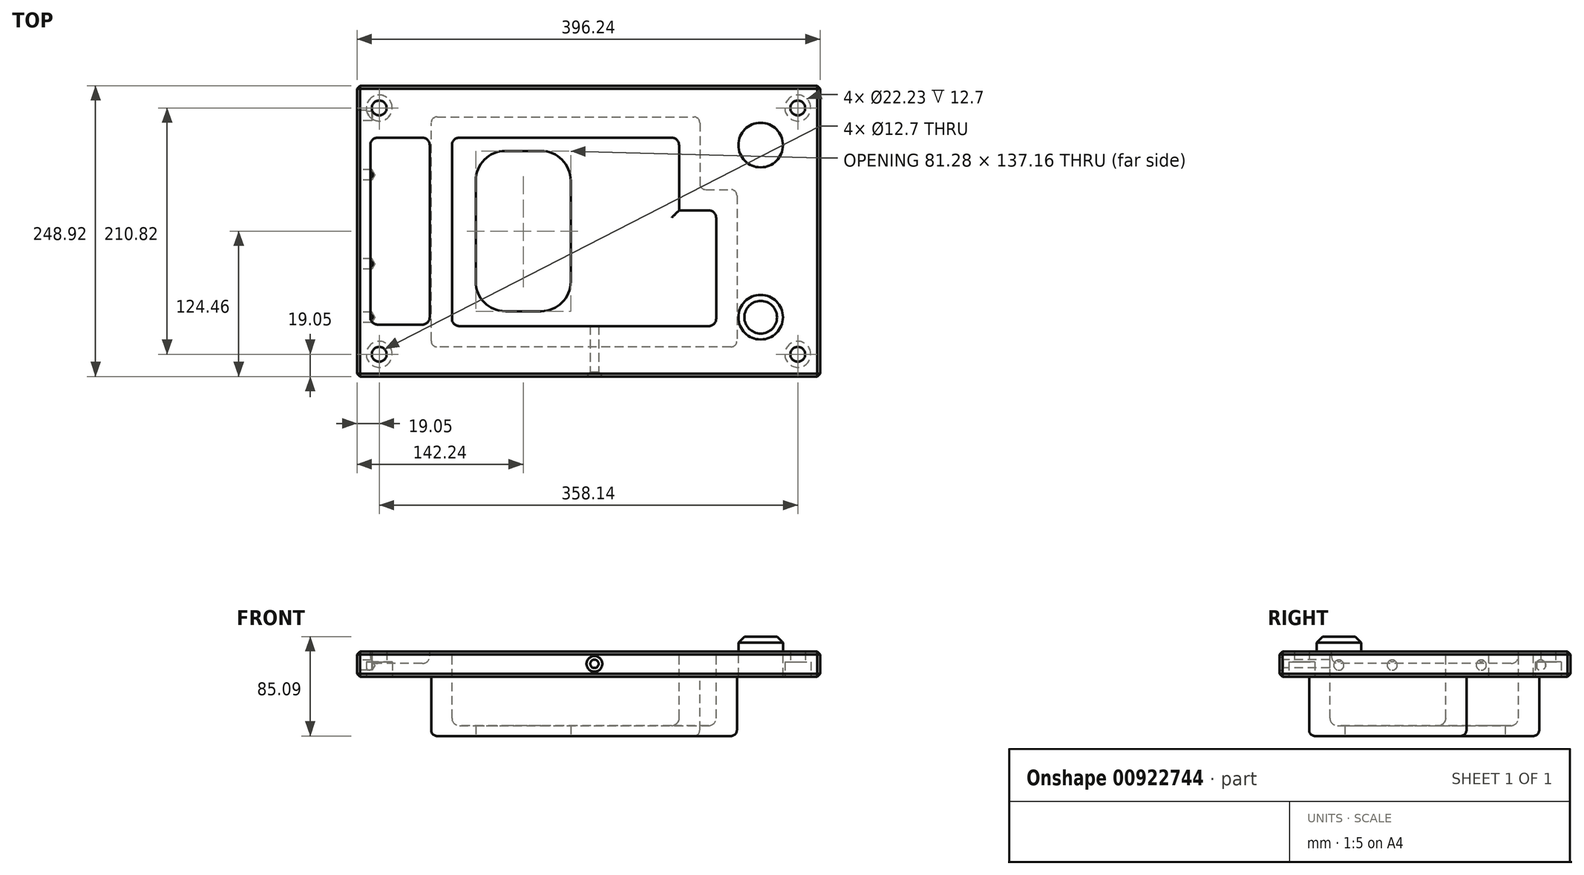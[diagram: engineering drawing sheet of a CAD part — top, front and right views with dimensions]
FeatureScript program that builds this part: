
annotation { "Feature Type Name" : "Feature", "Feature Type Description" : "" }
export const myFeature = defineFeature(function(context is Context, id is Id, definition is map)
    precondition{}
    {
        {
            var Q0;
            Q0=qCreatedBy(makeId("Top.planeOp"),FACE);
            var sketch = newSketch(context, id + "F0", { "sketchPlane" : qUnion([Q0])});
            skLineSegment(sketch, "E0.bottom", {"start": v(198.12, 124.46) * mm, "end": v(-198.12, 124.46) * mm});
            skLineSegment(sketch, "E0.top", {"start": v(198.12, -124.46) * mm, "end": v(-198.12, -124.46) * mm});
            skLineSegment(sketch, "E0.left", {"start": v(198.12, 124.46) * mm, "end": v(198.12, -124.46) * mm});
            skLineSegment(sketch, "E0.right", {"start": v(-198.12, 124.46) * mm, "end": v(-198.12, -124.46) * mm});
            skPoint(sketch, "E0.middle", {"position": v(0, 0) * mm});
            skSolve(sketch);
        }
        {
            var Q0;
            Q0=qSketchRegion(id+"F0",true);
            extrude(context, id + "F1", {"entities" : qUnion([Q0]), "oppositeDirection" : true, "depth" : 21.59 * mm, "offsetDistance" : 25.4 * mm});
        }
        {
            var Q0;
            Q0=makeQuery(id+"F1.opExtrude","CAP_FACE",FACE,{"disambiguationData":[OSD([sQuery(id+"F0.wireOp",EDGE,"E0.bottom"),sQuery(id+"F0.wireOp",EDGE,"E0.top"),sQuery(id+"F0.wireOp",EDGE,"E0.left"),sQuery(id+"F0.wireOp",EDGE,"E0.right")])],"isStart":false});
            var sketch = newSketch(context, id + "F2", { "sketchPlane" : qUnion([Q0])});
            skLineSegment(sketch, "E1", {"start": v(-134.62, 99.06) * mm, "end": v(-134.62, -97.79) * mm});
            skLineSegment(sketch, "E2", {"start": v(-134.62, -97.79) * mm, "end": v(95.25, -97.79) * mm});
            skLineSegment(sketch, "E3", {"start": v(95.25, -97.8) * mm, "end": v(95.25, -35.56) * mm});
            skLineSegment(sketch, "E4", {"start": v(95.25, -35.56) * mm, "end": v(127, -35.56) * mm});
            skLineSegment(sketch, "E5", {"start": v(127, -35.56) * mm, "end": v(127, 99.06) * mm});
            skLineSegment(sketch, "E6", {"start": v(127, 99.06) * mm, "end": v(-134.62, 99.06) * mm});
            skSolve(sketch);
        }
        {
            var Q0;
            Q0=qSketchRegion(id+"F2",true);
            extrude(context, id + "F3", {"entities" : qUnion([Q0]), "operationType" : NewBodyOperationType.ADD, "depth" : 50.8 * mm, "offsetDistance" : 25.4 * mm});
        }
        {
            var Q0;
            Q0=makeQuery(id+"F1.opExtrude","CAP_FACE",FACE,{"disambiguationData":[OSD([sQuery(id+"F0.wireOp",EDGE,"E0.bottom"),sQuery(id+"F0.wireOp",EDGE,"E0.top"),sQuery(id+"F0.wireOp",EDGE,"E0.left"),sQuery(id+"F0.wireOp",EDGE,"E0.right")])],"isStart":true});
            var sketch = newSketch(context, id + "F4", { "sketchPlane" : qUnion([Q0])});
            skLineSegment(sketch, "E7.0", {"start": v(127, -99.06) * mm, "end": v(-134.62, -99.06) * mm, "construction": true});
            skLineSegment(sketch, "E8.0", {"start": v(127, 35.56) * mm, "end": v(127, -99.06) * mm, "construction": true});
            skPoint(sketch, "E9.0", {"position": v(111.12, 35.56) * mm});
            skLineSegment(sketch, "E10.0", {"start": v(95.25, 97.8) * mm, "end": v(95.25, 35.56) * mm, "construction": true});
            skLineSegment(sketch, "E11.0", {"start": v(95.25, 35.56) * mm, "end": v(127, 35.56) * mm, "construction": true});
            skLineSegment(sketch, "E12.0", {"start": v(-134.62, 97.79) * mm, "end": v(95.25, 97.79) * mm, "construction": true});
            skLineSegment(sketch, "E13.0", {"start": v(-134.62, -99.06) * mm, "end": v(-134.62, 97.79) * mm, "construction": true});
            skLineSegment(sketch, "E14", {"start": v(109.22, -81.28) * mm, "end": v(109.22, 17.78) * mm});
            skLineSegment(sketch, "E15", {"start": v(109.22, 17.78) * mm, "end": v(77.47, 17.78) * mm});
            skLineSegment(sketch, "E16", {"start": v(77.47, 17.78) * mm, "end": v(77.47, 80) * mm});
            skLineSegment(sketch, "E17", {"start": v(77.47, 80) * mm, "end": v(-116.84, 80) * mm});
            skLineSegment(sketch, "E18", {"start": v(-116.84, 80) * mm, "end": v(-116.84, -81.28) * mm});
            skLineSegment(sketch, "E19", {"start": v(-116.84, -81.28) * mm, "end": v(109.22, -81.28) * mm});
            skSolve(sketch);
        }
        {
            var Q0;
            Q0=qSketchRegion(id+"F4",true);
            extrude(context, id + "F5", {"entities" : qUnion([Q0]), "operationType" : NewBodyOperationType.REMOVE, "oppositeDirection" : true, "depth" : 63.5 * mm, "offsetDistance" : 25.4 * mm});
        }
        {
            var Q0;
            Q0=makeQuery(id+"F5.boolean.opBoolean","COPY",FACE,{"derivedFrom":makeQuery(id+"F5.opExtrude","CAP_FACE",FACE,{"disambiguationData":[OSD([sQuery(id+"F4.wireOp",EDGE,"E14"),sQuery(id+"F4.wireOp",EDGE,"E15"),sQuery(id+"F4.wireOp",EDGE,"E16"),sQuery(id+"F4.wireOp",EDGE,"E17"),sQuery(id+"F4.wireOp",EDGE,"E18"),sQuery(id+"F4.wireOp",EDGE,"E19")])],"isStart":false})});
            var Q1;
            Q1=makeQuery(id+"F5.boolean.opBoolean","COPY",EDGE,{"derivedFrom":makeQuery(id+"F5.opExtrude","SWEPT_EDGE",EDGE,{"disambiguationData":[OSD([sQuery(id+"F4.wireOp",EDGE,"E14"),sQuery(id+"F4.wireOp",EDGE,"E19")])]})});
            var Q2;
            Q2=makeQuery(id+"F5.boolean.opBoolean","COPY",EDGE,{"derivedFrom":makeQuery(id+"F5.opExtrude","SWEPT_EDGE",EDGE,{"disambiguationData":[OSD([sQuery(id+"F4.wireOp",EDGE,"E18"),sQuery(id+"F4.wireOp",EDGE,"E19")])]})});
            var Q3;
            Q3=makeQuery(id+"F5.boolean.opBoolean","COPY",EDGE,{"derivedFrom":makeQuery(id+"F5.opExtrude","SWEPT_EDGE",EDGE,{"disambiguationData":[OSD([sQuery(id+"F4.wireOp",EDGE,"E17"),sQuery(id+"F4.wireOp",EDGE,"E18")])]})});
            var Q4;
            Q4=makeQuery(id+"F5.boolean.opBoolean","COPY",EDGE,{"derivedFrom":makeQuery(id+"F5.opExtrude","SWEPT_EDGE",EDGE,{"disambiguationData":[OSD([sQuery(id+"F4.wireOp",EDGE,"E14"),sQuery(id+"F4.wireOp",EDGE,"E15")])]})});
            var Q5;
            Q5=makeQuery(id+"F5.boolean.opBoolean","COPY",EDGE,{"derivedFrom":makeQuery(id+"F5.opExtrude","SWEPT_EDGE",EDGE,{"disambiguationData":[OSD([sQuery(id+"F4.wireOp",EDGE,"E16"),sQuery(id+"F4.wireOp",EDGE,"E17")])]})});
            fillet(context, id + "F6", {"entities" : qUnion([Q0, Q1, Q2, Q3, Q4, Q5]), "radius" : 6.35 * mm, "tangentPropagation" : true, "allowEdgeOverflow" : false});
        }
        {
            var Q0;
            Q0=makeQuery(id+"F3.opExtrude","SWEPT_EDGE",EDGE,{"disambiguationData":[OSD([sQuery(id+"F2.wireOp",EDGE,"E3"),sQuery(id+"F2.wireOp",EDGE,"E4")])]});
            fillet(context, id + "F7", {"entities" : qUnion([Q0]), "radius" : 5.08 * mm, "tangentPropagation" : true, "allowEdgeOverflow" : false});
        }
        {
            var Q0;
            Q0=makeQuery(id+"F3.opExtrude","CAP_FACE",FACE,{"disambiguationData":[OSD([sQuery(id+"F2.wireOp",EDGE,"E1"),sQuery(id+"F2.wireOp",EDGE,"E2"),sQuery(id+"F2.wireOp",EDGE,"E3"),sQuery(id+"F2.wireOp",EDGE,"E4"),sQuery(id+"F2.wireOp",EDGE,"E5"),sQuery(id+"F2.wireOp",EDGE,"E6")])],"isStart":false});
            var sketch = newSketch(context, id + "F8", { "sketchPlane" : qUnion([Q0])});
            skLineSegment(sketch, "E20.bottom", {"start": v(-96.52, -68.58) * mm, "end": v(-15.24, -68.58) * mm});
            skLineSegment(sketch, "E20.top", {"start": v(-96.52, 68.58) * mm, "end": v(-15.24, 68.58) * mm});
            skLineSegment(sketch, "E20.left", {"start": v(-96.52, -68.58) * mm, "end": v(-96.52, 68.58) * mm});
            skLineSegment(sketch, "E20.right", {"start": v(-15.24, -68.58) * mm, "end": v(-15.24, 68.58) * mm});
            skPoint(sketch, "E20.middle", {"position": v(-55.88, 0) * mm});
            skSolve(sketch);
        }
        {
            var Q0;
            Q0=qSketchRegion(id+"F8",true);
            extrude(context, id + "F9", {"entities" : qUnion([Q0]), "operationType" : NewBodyOperationType.REMOVE, "endBound" : BoundingType.THROUGH_ALL, "oppositeDirection" : true, "depth" : 25.4 * mm, "offsetDistance" : 25.4 * mm});
        }
        {
            var Q0;
            Q0=makeQuery(id+"F1.opExtrude","CAP_FACE",FACE,{"disambiguationData":[OSD([sQuery(id+"F0.wireOp",EDGE,"E0.bottom"),sQuery(id+"F0.wireOp",EDGE,"E0.top"),sQuery(id+"F0.wireOp",EDGE,"E0.left"),sQuery(id+"F0.wireOp",EDGE,"E0.right")])],"isStart":true});
            var sketch = newSketch(context, id + "F10", { "sketchPlane" : qUnion([Q0])});
            skLineSegment(sketch, "E21.bottom", {"start": v(-135.9, 80) * mm, "end": v(-186.7, 80) * mm});
            skLineSegment(sketch, "E21.top", {"start": v(-135.9, -80) * mm, "end": v(-186.7, -80) * mm});
            skLineSegment(sketch, "E21.left", {"start": v(-135.9, 80) * mm, "end": v(-135.9, -80) * mm});
            skLineSegment(sketch, "E21.right", {"start": v(-186.7, 80) * mm, "end": v(-186.7, -80) * mm});
            skPoint(sketch, "E21.middle", {"position": v(-161.3, 0) * mm});
            skSolve(sketch);
        }
        {
            var Q0;
            Q0=qSketchRegion(id+"F10",true);
            extrude(context, id + "F11", {"entities" : qUnion([Q0]), "operationType" : NewBodyOperationType.REMOVE, "oppositeDirection" : true, "depth" : 10.4 * mm, "offsetDistance" : 25.4 * mm});
        }
        {
            var Q0;
            Q0=makeQuery(id+"F11.boolean.opBoolean","COPY",FACE,{"derivedFrom":makeQuery(id+"F11.opExtrude","CAP_FACE",FACE,{"disambiguationData":[OSD([sQuery(id+"F10.wireOp",EDGE,"E21.bottom"),sQuery(id+"F10.wireOp",EDGE,"E21.top"),sQuery(id+"F10.wireOp",EDGE,"E21.left"),sQuery(id+"F10.wireOp",EDGE,"E21.right")])],"isStart":false})});
            var Q1;
            Q1=makeQuery(id+"F11.boolean.opBoolean","COPY",EDGE,{"derivedFrom":makeQuery(id+"F11.opExtrude","SWEPT_EDGE",EDGE,{"disambiguationData":[OSD([sQuery(id+"F10.wireOp",EDGE,"E21.bottom"),sQuery(id+"F10.wireOp",EDGE,"E21.right")])]})});
            var Q2;
            Q2=makeQuery(id+"F11.boolean.opBoolean","COPY",EDGE,{"derivedFrom":makeQuery(id+"F11.opExtrude","SWEPT_EDGE",EDGE,{"disambiguationData":[OSD([sQuery(id+"F10.wireOp",EDGE,"E21.bottom"),sQuery(id+"F10.wireOp",EDGE,"E21.left")])]})});
            var Q3;
            Q3=makeQuery(id+"F11.boolean.opBoolean","COPY",EDGE,{"derivedFrom":makeQuery(id+"F11.opExtrude","SWEPT_EDGE",EDGE,{"disambiguationData":[OSD([sQuery(id+"F10.wireOp",EDGE,"E21.top"),sQuery(id+"F10.wireOp",EDGE,"E21.left")])]})});
            var Q4;
            Q4=makeQuery(id+"F11.boolean.opBoolean","COPY",EDGE,{"derivedFrom":makeQuery(id+"F11.opExtrude","SWEPT_EDGE",EDGE,{"disambiguationData":[OSD([sQuery(id+"F10.wireOp",EDGE,"E21.top"),sQuery(id+"F10.wireOp",EDGE,"E21.right")])]})});
            fillet(context, id + "F12", {"entities" : qUnion([Q0, Q1, Q2, Q3, Q4]), "radius" : 6.35 * mm, "tangentPropagation" : true, "allowEdgeOverflow" : false});
        }
        {
            var Q0;
            Q0=makeQuery(id+"F1.opExtrude","CAP_FACE",FACE,{"disambiguationData":[OSD([sQuery(id+"F0.wireOp",EDGE,"E0.bottom"),sQuery(id+"F0.wireOp",EDGE,"E0.top"),sQuery(id+"F0.wireOp",EDGE,"E0.left"),sQuery(id+"F0.wireOp",EDGE,"E0.right")])],"isStart":true});
            var sketch = newSketch(context, id + "F13", { "sketchPlane" : qUnion([Q0])});
            skLineSegment(sketch, "E22.bottom", {"start": v(160.02, 86.36) * mm, "end": v(134.62, 86.36) * mm});
            skLineSegment(sketch, "E22.top", {"start": v(160.02, 60.96) * mm, "end": v(134.62, 60.96) * mm});
            skLineSegment(sketch, "E22.left", {"start": v(160.02, 86.36) * mm, "end": v(160.02, 60.96) * mm});
            skLineSegment(sketch, "E22.right", {"start": v(134.62, 86.36) * mm, "end": v(134.62, 60.96) * mm});
            skPoint(sketch, "E22.middle", {"position": v(147.32, 73.66) * mm});
            skCircle(sketch, "E23", {"center": v(147.32, -73.66) * mm, "radius": 19.05 * mm});
            skSolve(sketch);
        }
        {
            var Q0;
            Q0=makeQuery(id+"F13.imprint","IMPRINT",FACE,{"disambiguationData":[TD([[makeQuery(id+"F13.imprint","IMPRINT",EDGE,{"derivedFrom":sQuery(id+"F13.wireOp",EDGE,"E23")}),1.0]])]});
            extrude(context, id + "F14", {"entities" : qUnion([Q0]), "operationType" : NewBodyOperationType.ADD, "depth" : 12.7 * mm, "offsetDistance" : 25.4 * mm});
        }
        {
            var Q0;
            Q0=makeQuery(id+"F14.opExtrude","CAP_FACE",FACE,{"disambiguationData":[OSD([sQuery(id+"F13.wireOp",EDGE,"E22.bottom"),sQuery(id+"F13.wireOp",EDGE,"E22.top"),sQuery(id+"F13.wireOp",EDGE,"E22.left"),sQuery(id+"F13.wireOp",EDGE,"E22.right")])],"isStart":false});
            var Q1;
            Q1=makeQuery(id+"F14.opExtrude","CAP_FACE",FACE,{"disambiguationData":[OSD([sQuery(id+"F13.wireOp",EDGE,"E23")])],"isStart":false});
            chamfer(context, id + "F15", {"entities" : qUnion([Q0, Q1]), "width" : 5.08 * mm, "tangentPropagation" : true});
        }
        {
            var Q0;
            Q0=makeQuery(id+"F1.opExtrude","SWEPT_FACE",FACE,{"disambiguationData":[OSD([sQuery(id+"F0.wireOp",EDGE,"E0.top")])]});
            var sketch = newSketch(context, id + "F16", { "sketchPlane" : qUnion([Q0])});
            skPoint(sketch, "E24", {"position": v(5.08, -10.67) * mm});
            skSolve(sketch);
        }
        {
            var Q0;
            Q0=sQuery(id+"F16.wireOp",VERTEX,"E24");
            var Q1;
            Q1=makeQuery(id+"F1.opExtrude","SWEPT_BODY",BODY,{"disambiguationData":[OSD([sQuery(id+"F0.wireOp",EDGE,"E0.bottom"),sQuery(id+"F0.wireOp",EDGE,"E0.top"),sQuery(id+"F0.wireOp",EDGE,"E0.left"),sQuery(id+"F0.wireOp",EDGE,"E0.right")])]});
            hole(context, id + "F17", {"style" : HoleStyle.C_SINK, "endStyle" : HoleEndStyle.BLIND, "standardTappedOrClearance" : lookupTablePath({ "fit" : "Normal (ASME)", "standard" : "ANSI", "size" : "1/4", "type" : "Clearance" }), "standardBlindInLast" : lookupTablePath({ "fit" : "Normal", "standard" : "ANSI", "size" : "1/4", "type" : "Clearance" }), "holeDiameter" : 7.14 * mm, "cSinkDiameter" : 13.5 * mm, "cSinkAngle" : 82 * degree, "majorDiameter" : 6.35 * mm, "holeDepth" : 127 * mm, "isTappedThrough" : true, "tappedDepth" : 12.7 * mm, "tapClearance" : 3, "locations" : qUnion([Q0]), "scope" : qUnion([Q1])});
        }
        {
            var Q0;
            Q0=makeQuery(id+"F3.opExtrude","CAP_EDGE",EDGE,{"disambiguationData":[OSD([sQuery(id+"F2.wireOp",EDGE,"E6")])],"isStart":false});
            var Q1;
            Q1=makeQuery(id+"F3.opExtrude","SWEPT_EDGE",EDGE,{"disambiguationData":[OSD([sQuery(id+"F2.wireOp",EDGE,"E1"),sQuery(id+"F2.wireOp",EDGE,"E6")])]});
            var Q2;
            Q2=makeQuery(id+"F3.opExtrude","CAP_EDGE",EDGE,{"disambiguationData":[OSD([sQuery(id+"F2.wireOp",EDGE,"E1")])],"isStart":false});
            var Q3;
            Q3=makeQuery(id+"F3.opExtrude","CAP_EDGE",EDGE,{"disambiguationData":[OSD([sQuery(id+"F2.wireOp",EDGE,"E5")])],"isStart":false});
            var Q4;
            Q4=makeQuery(id+"F3.opExtrude","SWEPT_EDGE",EDGE,{"disambiguationData":[OSD([sQuery(id+"F2.wireOp",EDGE,"E5"),sQuery(id+"F2.wireOp",EDGE,"E6")])]});
            var Q5;
            Q5=makeQuery(id+"F3.opExtrude","SWEPT_EDGE",EDGE,{"disambiguationData":[OSD([sQuery(id+"F2.wireOp",EDGE,"E4"),sQuery(id+"F2.wireOp",EDGE,"E5")])]});
            var Q6;
            Q6=makeQuery(id+"F3.opExtrude","CAP_EDGE",EDGE,{"disambiguationData":[OSD([sQuery(id+"F2.wireOp",EDGE,"E4")])],"isStart":false});
            var Q7;
            Q7=makeQuery(id+"F3.opExtrude","SWEPT_EDGE",EDGE,{"disambiguationData":[OSD([sQuery(id+"F2.wireOp",EDGE,"E2"),sQuery(id+"F2.wireOp",EDGE,"E3")])]});
            var Q8;
            Q8=makeQuery(id+"F3.opExtrude","CAP_EDGE",EDGE,{"disambiguationData":[OSD([sQuery(id+"F2.wireOp",EDGE,"E2")])],"isStart":false});
            var Q9;
            Q9=makeQuery(id+"F3.opExtrude","SWEPT_EDGE",EDGE,{"disambiguationData":[OSD([sQuery(id+"F2.wireOp",EDGE,"E1"),sQuery(id+"F2.wireOp",EDGE,"E2")])]});
            fillet(context, id + "F18", {"entities" : qUnion([Q0, Q1, Q2, Q3, Q4, Q5, Q6, Q7, Q8, Q9]), "radius" : 5.08 * mm, "tangentPropagation" : true, "allowEdgeOverflow" : false});
        }
        {
            var Q0;
            Q0=makeQuery(id+"F2.imprint","IMPRINT",FACE,{"disambiguationData":[TD([[makeQuery(id+"F2.imprint","IMPRINT",EDGE,{"derivedFrom":sQuery(id+"F2.wireOp",EDGE,"E1")}),-1.0]])]});
            var sketch = newSketch(context, id + "F19", { "sketchPlane" : qUnion([Q0])});
            skLineSegment(sketch, "E25.bottom", {"start": v(179.07, -105.41) * mm, "end": v(-179.07, -105.41) * mm});
            skLineSegment(sketch, "E25.top", {"start": v(179.07, 105.41) * mm, "end": v(-179.07, 105.41) * mm});
            skLineSegment(sketch, "E25.left", {"start": v(179.07, -105.41) * mm, "end": v(179.07, 105.41) * mm});
            skLineSegment(sketch, "E25.right", {"start": v(-179.07, -105.41) * mm, "end": v(-179.07, 105.41) * mm});
            skPoint(sketch, "E25.middle", {"position": v(0, 0) * mm});
            skSolve(sketch);
        }
        {
            var Q0;
            Q0=sQuery(id+"F19.wireOp",VERTEX,"E25.top.end");
            var Q1;
            Q1=sQuery(id+"F19.wireOp",VERTEX,"E25.top.start");
            var Q2;
            Q2=sQuery(id+"F19.wireOp",VERTEX,"E25.bottom.start");
            var Q3;
            Q3=sQuery(id+"F19.wireOp",VERTEX,"E25.bottom.end");
            var Q4;
            Q4=makeQuery(id+"F1.opExtrude","SWEPT_BODY",BODY,{"disambiguationData":[OSD([sQuery(id+"F0.wireOp",EDGE,"E0.bottom"),sQuery(id+"F0.wireOp",EDGE,"E0.top"),sQuery(id+"F0.wireOp",EDGE,"E0.left"),sQuery(id+"F0.wireOp",EDGE,"E0.right")])]});
            hole(context, id + "F20", {"style" : HoleStyle.C_BORE, "endStyle" : HoleEndStyle.THROUGH, "holeDiameter" : 12.7 * mm, "cBoreDiameter" : 22.22 * mm, "cBoreDepth" : 12.7 * mm, "majorDiameter" : 6.35 * mm, "isTappedThrough" : true, "tappedDepth" : 12.7 * mm, "tapClearance" : 3, "locations" : qUnion([Q0, Q1, Q2, Q3]), "scope" : qUnion([Q4])});
        }
        {
            var Q0;
            Q0=makeQuery(id+"F1.opExtrude","CAP_FACE",FACE,{"disambiguationData":[OSD([sQuery(id+"F0.wireOp",EDGE,"E0.bottom"),sQuery(id+"F0.wireOp",EDGE,"E0.top"),sQuery(id+"F0.wireOp",EDGE,"E0.left"),sQuery(id+"F0.wireOp",EDGE,"E0.right")])],"isStart":true});
            var sketch = newSketch(context, id + "F21", { "sketchPlane" : qUnion([Q0])});
            skCircle(sketch, "E26", {"center": v(147.32, 73.66) * mm, "radius": 19.05 * mm});
            skSolve(sketch);
        }
        {
            var Q0;
            Q0=qSketchRegion(id+"F21",true);
            extrude(context, id + "F22", {"entities" : qUnion([Q0]), "operationType" : NewBodyOperationType.REMOVE, "endBound" : BoundingType.THROUGH_ALL, "oppositeDirection" : true, "depth" : 25.4 * mm, "offsetDistance" : 25.4 * mm});
        }
        {
            var Q0;
            Q0=makeQuery(id+"F1.opExtrude","SWEPT_FACE",FACE,{"disambiguationData":[OSD([sQuery(id+"F0.wireOp",EDGE,"E0.right")])]});
            var sketch = newSketch(context, id + "F23", { "sketchPlane" : qUnion([Q0])});
            skLineSegment(sketch, "E27", {"start": v(-99.06, -11.75) * mm, "end": v(73.66, -11.75) * mm, "construction": true});
            skPoint(sketch, "E28", {"position": v(-48.26, -11.75) * mm});
            skPoint(sketch, "E29", {"position": v(27.94, -11.75) * mm});
            skSolve(sketch);
        }
        {
            var Q0;
            Q0=makeQuery(id+"F1.opExtrude","SWEPT_FACE",FACE,{"disambiguationData":[OSD([sQuery(id+"F0.wireOp",EDGE,"E0.bottom")])]});
            var Q1;
            Q1=makeQuery(id+"F1.opExtrude","SWEPT_FACE",FACE,{"disambiguationData":[OSD([sQuery(id+"F0.wireOp",EDGE,"E0.left")])]});
            var Q2;
            Q2=makeQuery(id+"F1.opExtrude","SWEPT_FACE",FACE,{"disambiguationData":[OSD([sQuery(id+"F0.wireOp",EDGE,"E0.right")])]});
            var Q3;
            Q3=makeQuery(id+"F5.boolean.opBoolean","COPY",EDGE,{"derivedFrom":makeQuery(id+"F5.opExtrude","CAP_EDGE",EDGE,{"disambiguationData":[OSD([sQuery(id+"F4.wireOp",EDGE,"E15")])],"isStart":true})});
            var Q4;
            Q4=makeQuery(id+"F1.opExtrude","CAP_EDGE",EDGE,{"disambiguationData":[OSD([sQuery(id+"F0.wireOp",EDGE,"E0.top")])],"isStart":false});
            var Q5;
            Q5=makeQuery(id+"F1.opExtrude","CAP_EDGE",EDGE,{"disambiguationData":[OSD([sQuery(id+"F0.wireOp",EDGE,"E0.top")])],"isStart":true});
            chamfer(context, id + "F24", {"entities" : qUnion([Q0, Q1, Q2, Q3, Q4, Q5]), "width" : 2.54 * mm, "tangentPropagation" : true});
        }
        {
            var Q0;
            Q0=makeQuery(id+"F9.boolean.opBoolean","COPY",EDGE,{"derivedFrom":makeQuery(id+"F9.opExtrude","SWEPT_EDGE",EDGE,{"disambiguationData":[OSD([sQuery(id+"F8.wireOp",EDGE,"E20.top"),sQuery(id+"F8.wireOp",EDGE,"E20.right")])]})});
            var Q1;
            Q1=makeQuery(id+"F9.boolean.opBoolean","COPY",EDGE,{"derivedFrom":makeQuery(id+"F9.opExtrude","SWEPT_EDGE",EDGE,{"disambiguationData":[OSD([sQuery(id+"F8.wireOp",EDGE,"E20.bottom"),sQuery(id+"F8.wireOp",EDGE,"E20.right")])]})});
            var Q2;
            Q2=makeQuery(id+"F9.boolean.opBoolean","COPY",EDGE,{"derivedFrom":makeQuery(id+"F9.opExtrude","SWEPT_EDGE",EDGE,{"disambiguationData":[OSD([sQuery(id+"F8.wireOp",EDGE,"E20.bottom"),sQuery(id+"F8.wireOp",EDGE,"E20.left")])]})});
            var Q3;
            Q3=makeQuery(id+"F9.boolean.opBoolean","COPY",EDGE,{"derivedFrom":makeQuery(id+"F9.opExtrude","SWEPT_EDGE",EDGE,{"disambiguationData":[OSD([sQuery(id+"F8.wireOp",EDGE,"E20.top"),sQuery(id+"F8.wireOp",EDGE,"E20.left")])]})});
            fillet(context, id + "F25", {"entities" : qUnion([Q0, Q1, Q2, Q3]), "radius" : 25.4 * mm, "tangentPropagation" : true, "allowEdgeOverflow" : false});
        }
        {
            var Q0;
            Q0=sQuery(id+"F23.wireOp",VERTEX,"E28");
            var Q1;
            Q1=sQuery(id+"F23.wireOp",VERTEX,"E29");
            var Q2;
            Q2=sQuery(id+"F23.wireOp",VERTEX,"E27.end");
            var Q3;
            Q3=sQuery(id+"F23.wireOp",VERTEX,"E27.start");
            var Q4;
            Q4=makeQuery(id+"F1.opExtrude","SWEPT_BODY",BODY,{"disambiguationData":[OSD([sQuery(id+"F0.wireOp",EDGE,"E0.bottom"),sQuery(id+"F0.wireOp",EDGE,"E0.top"),sQuery(id+"F0.wireOp",EDGE,"E0.left"),sQuery(id+"F0.wireOp",EDGE,"E0.right")])]});
            hole(context, id + "F26", {"style" : HoleStyle.SIMPLE, "endStyle" : HoleEndStyle.BLIND, "standardTappedOrClearance" : lookupTablePath({ "fit" : "Normal (ASME)", "standard" : "ANSI", "size" : "5/16", "type" : "Clearance" }), "standardBlindInLast" : lookupTablePath({ "fit" : "Normal", "standard" : "ANSI", "size" : "5/16", "type" : "Clearance" }), "holeDiameter" : 8.74 * mm, "majorDiameter" : 6.35 * mm, "holeDepth" : 12.7 * mm, "isTappedThrough" : true, "tappedDepth" : 12.7 * mm, "tapClearance" : 3, "locations" : qUnion([Q0, Q1, Q2, Q3]), "scope" : qUnion([Q4])});
        }
    });
